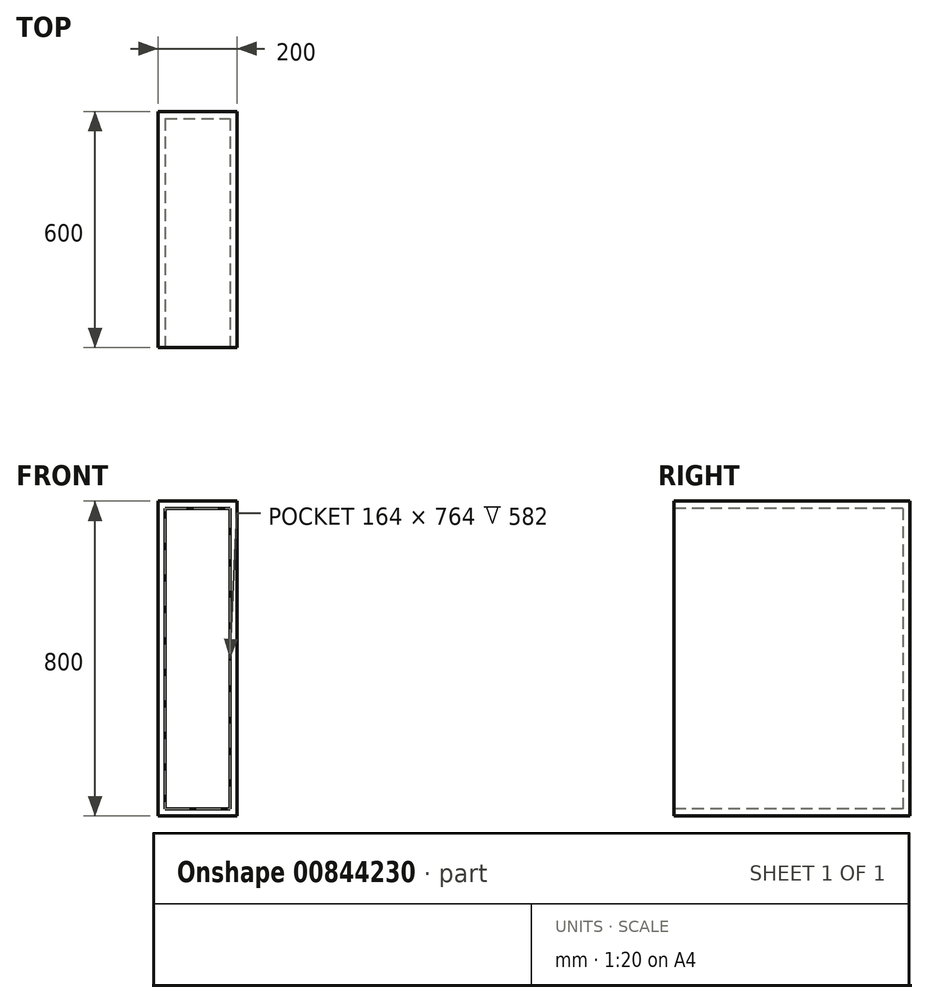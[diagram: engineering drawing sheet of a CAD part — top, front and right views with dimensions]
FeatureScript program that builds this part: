
annotation { "Feature Type Name" : "Feature", "Feature Type Description" : "" }
export const myFeature = defineFeature(function(context is Context, id is Id, definition is map)
    precondition{}
    {
        {
            var Q0;
            Q0=qCreatedBy(makeId("Top.planeOp"),FACE);
            var sketch = newSketch(context, id + "F0", { "sketchPlane" : qUnion([Q0])});
            skLineSegment(sketch, "E0.bottom", {"start": v(0, 0) * mm, "end": v(43.04, 0) * mm});
            skLineSegment(sketch, "E0.top", {"start": v(0, -43.78) * mm, "end": v(43.04, -43.78) * mm});
            skLineSegment(sketch, "E0.left", {"start": v(0, 0) * mm, "end": v(0, -43.78) * mm});
            skLineSegment(sketch, "E0.right", {"start": v(43.04, 0) * mm, "end": v(43.04, -43.78) * mm});
            skSolve(sketch);
        }
        {
            var Q0;
            Q0=makeQuery(id+"F0.imprint","IMPRINT",FACE,{"disambiguationData":[TD([[makeQuery(id+"F0.imprint","IMPRINT",EDGE,{"derivedFrom":sQuery(id+"F0.wireOp",EDGE,"E0.bottom")}),-1.0]])]});
            extrude(context, id + "F1", {"entities" : qUnion([Q0]), "depth" : 800 * mm, "offsetDistance" : 25 * mm});
        }
        {
            var Q0;
            Q0=makeQuery(id+"F1.opExtrude","SWEPT_FACE",FACE,{"disambiguationData":[OSD([sQuery(id+"F0.wireOp",EDGE,"E0.left")])]});
            extrude(context, id + "F2", {"entities" : qUnion([Q0]), "operationType" : NewBodyOperationType.ADD, "oppositeDirection" : true, "depth" : 200 * mm, "offsetDistance" : 25 * mm});
        }
        {
            var Q0;
            {var subQ0=sQuery(id+"F0.wireOp",EDGE,"E0.top");Q0=makeQuery(id+"F2.boolean.opBoolean","MERGE",FACE,{"derivedFrom":[makeQuery(id+"F1.opExtrude","SWEPT_FACE",FACE,{"disambiguationData":[OSD([subQ0])]}),makeQuery(id+"F2.opExtrude","SWEPT_FACE",FACE,{"disambiguationData":[OSD([subQ0,sQuery(id+"F0.wireOp",EDGE,"E0.left")])]})]});}
            extrude(context, id + "F3", {"entities" : qUnion([Q0]), "operationType" : NewBodyOperationType.ADD, "oppositeDirection" : true, "depth" : 600 * mm, "offsetDistance" : 25 * mm});
        }
        {
            var Q0;
            {var subQ0=sQuery(id+"F0.wireOp",EDGE,"E0.top");Q0=makeQuery(id+"F2.boolean.opBoolean","MERGE",FACE,{"derivedFrom":[makeQuery(id+"F1.opExtrude","SWEPT_FACE",FACE,{"disambiguationData":[OSD([subQ0])]}),makeQuery(id+"F2.opExtrude","SWEPT_FACE",FACE,{"disambiguationData":[OSD([subQ0,sQuery(id+"F0.wireOp",EDGE,"E0.left")])]})]});}
            shell(context, id + "F4", {"entities" : qUnion([Q0]), "thickness" : 18 * mm});
        }
    });
